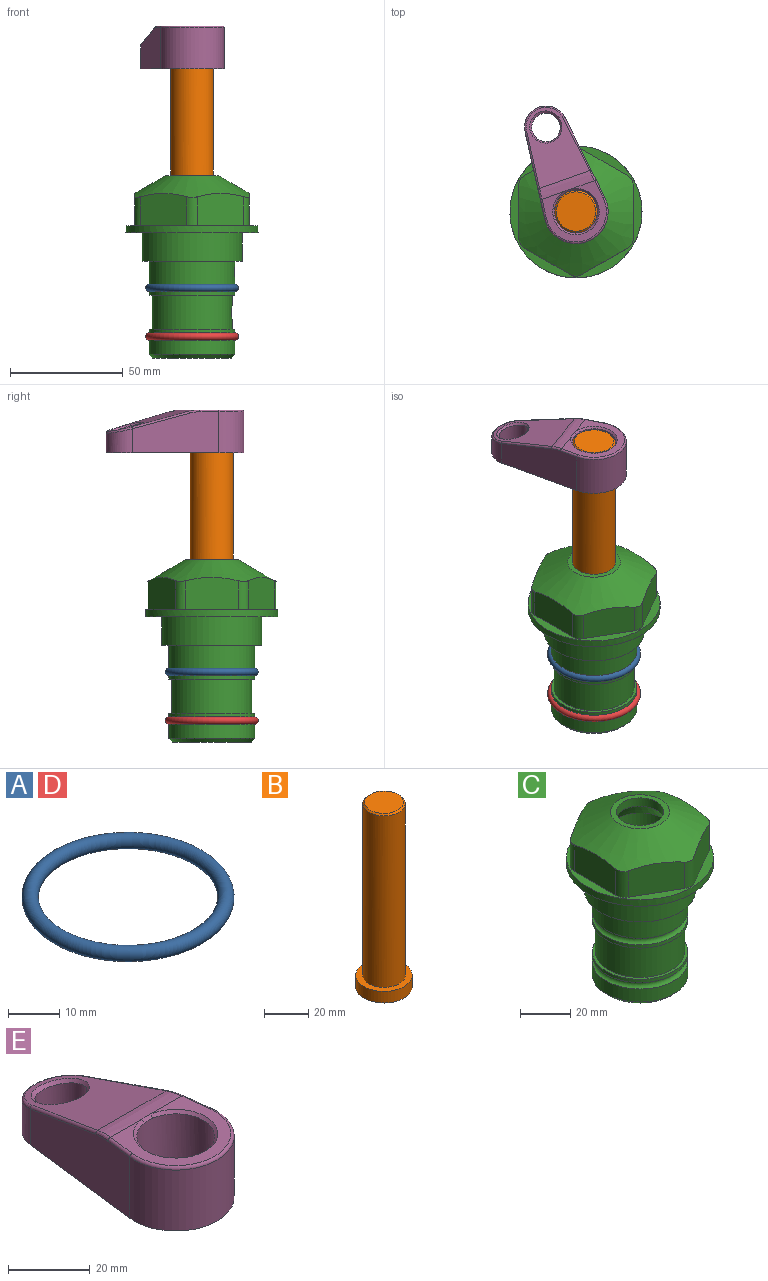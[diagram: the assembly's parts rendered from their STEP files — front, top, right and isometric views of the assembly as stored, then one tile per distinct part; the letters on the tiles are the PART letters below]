
ASSEMBLY  parts=5 mates=4
PART A: 1 faces, bbox 44.7x44.7x3.2 mm
  f0: torus R=19.05mm, axis (0,0,1), area 1193.9mm2
PART B: 6 faces, bbox 25.4x25.4x101.6 mm
  f0: plane 17.46x17.46mm, normal (0,0,1), area 239.5mm2, adj f5
  f1: plane 25.4x25.4mm, normal (0,0,-1), area 506.7mm2, adj f2
  f2: cylinder r=12.7mm len=25.4mm, axis (0,0,1), area 506.7mm2, adj f1,f3
  f3: plane 25.4x25.4mm, normal (0,0,1), area 221.7mm2, adj f2,f4
  f4: cylinder r=9.53mm len=94.46mm, axis (0,0,1), area 5653mm2, adj f3,f5
  f5: cone r=8.73mm half-angle=45deg, axis (0,0,-1), area 64.4mm2, adj f0,f4
PART C: 36 faces, bbox 58.7x58.7x81 mm
  f0: cylinder r=17.78mm len=35.56mm, axis (0,0,1), area 1670.8mm2, adj f23,f24,f31
  f1: cylinder r=19.05mm len=38.1mm, axis (0,0,1), area 1191.9mm2, adj f26,f27,f30
  f2: plane 58.66x58.66mm, normal (0,0,-1), area 1150.6mm2, adj f3,f28
  f3: cylinder r=29.33mm len=58.66mm, axis (0,0,-1), area 585.1mm2, adj f2,f4
  f4: plane 58.66x58.66mm, normal (0,0,1), area 475.9mm2, adj f3,f5,f6,f7,f8,f9,f10,f11
  f5: plane 20.32x14.34mm, normal (-0.5,0.87,0), area 324.4mm2, adj f4,f15,f16,f17
  f6: plane 20.32x14.34mm, normal (0.5,0.87,0), area 324.4mm2, adj f4,f14,f15,f17
  f7: plane 23.48x14.34mm, normal (1,0,0), area 324.4mm2, adj f4,f13,f14,f17
  f8: plane 20.32x14.34mm, normal (0.5,-0.87,0), area 324.4mm2, adj f4,f12,f13,f17
  f9: plane 20.32x14.34mm, normal (-0.5,-0.87,0), area 324.4mm2, adj f4,f11,f12,f17
  f10: plane 23.48x14.34mm, normal (-1,0,0), area 324.4mm2, adj f4,f11,f16,f17
  f11: cylinder r=5.08mm len=12.85mm, axis (0,0,-1), area 67.2mm2, adj f4,f9,f10,f17
  f12: cylinder r=5.08mm len=12.85mm, axis (0,0,-1), area 67.2mm2, adj f4,f8,f9,f17
  f13: cylinder r=5.08mm len=12.85mm, axis (0,0,-1), area 67.2mm2, adj f4,f7,f8,f17
  f14: cylinder r=5.08mm len=12.85mm, axis (0,0,-1), area 67.2mm2, adj f4,f6,f7,f17
  f15: cylinder r=5.08mm len=12.85mm, axis (0,0,-1), area 67.2mm2, adj f4,f5,f6,f17
  f16: cylinder r=5.08mm len=12.85mm, axis (0,0,-1), area 67.2mm2, adj f4,f5,f10,f17
  f17: cone r=11.73mm half-angle=60deg, axis (0,0,-1), area 2071.8mm2, adj f5,f6,f7,f8,f9,f10,f11,f12
  f18: plane 23.46x23.46mm, normal (0,0,1), area 147.4mm2, adj f17,f35
  f19: plane 34.93x34.93mm, normal (0,0,-1), area 958mm2, adj f29
  f20: cylinder r=19.05mm len=38.1mm, axis (0,0,1), area 760.1mm2, adj f21,f29
  f21: torus R=19.05mm, axis (0,0,1), area 565.3mm2, adj f20,f22
  f22: cylinder r=19.05mm len=38.1mm, axis (0,0,1), area 190mm2, adj f21,f23
  f23: plane 38.1x38.1mm, normal (0,0,1), area 146.9mm2, adj f0,f22
  f24: plane 38.1x38.1mm, normal (0,0,-1), area 146.9mm2, adj f0,f25
  f25: cylinder r=19.05mm len=38.1mm, axis (0,0,1), area 190mm2, adj f24,f26
  f26: torus R=19.05mm, axis (0,0,1), area 565.3mm2, adj f1,f25
  f27: plane 44.45x44.45mm, normal (0,0,-1), area 411.7mm2, adj f1,f28
  f28: cylinder r=22.23mm len=44.45mm, axis (0,0,1), area 1773.5mm2, adj f2,f27
  f29: cone r=19.05mm half-angle=45deg, axis (0,0,1), area 257.5mm2, adj f19,f20
  f30: cylinder r=3.17mm len=6.75mm, axis (-1,0,0), area 128mm2, adj f1,f33
  f31: cylinder r=3.17mm len=6.35mm, axis (-1,0,0), area 102.5mm2, adj f0,f33
  f32: plane 25.4x25.4mm, normal (0,0,1), area 506.7mm2, adj f33
  f33: cylinder r=12.7mm len=66.42mm, axis (0,0,-1), area 5236.2mm2, adj f30,f31,f32,f34
  f34: cone r=9.53mm half-angle=30deg, axis (0,0,-1), area 443.4mm2, adj f33,f35
  f35: cylinder r=9.53mm len=19.05mm, axis (0,0,-1), area 240.9mm2, adj f18,f34
PART D: same geometry as A
PART E: 31 faces, bbox 31.7x65.5x19.8 mm
  f0: plane 39.12x18.26mm, normal (0.99,0.12,0), area 612.2mm2, adj f1,f4,f7,f11,f13,f15
  f1: cylinder r=9.53mm len=18.91mm, axis (0,0,-1), area 296.1mm2, adj f0,f2,f7,f17
  f2: plane 39.12x18.26mm, normal (-0.99,0.12,0), area 612.2mm2, adj f1,f4,f7,f12,f14,f16
  f3: cylinder r=6.35mm len=12.7mm, axis (0,0,-1), area 362.4mm2, adj f7,f18
  f4: cylinder r=14.29mm len=28.58mm, axis (0,0,-1), area 882.2mm2, adj f0,f2,f7,f10
  f5: cylinder r=9.53mm len=19.05mm, axis (0,0,-1), area 1092.6mm2, adj f7,f19,f20
  f6: plane 26.99x23.69mm, normal (0,0,1), area 216.2mm2, adj f9,f10,f11,f12,f19
  f7: plane 63.5x28.58mm, normal (0,0,-1), area 661.8mm2, adj f0,f1,f2,f3,f4,f5,f22,f23
  f8: plane 33.52x23.6mm, normal (0,0.26,0.97), area 486mm2, adj f9,f15,f16,f17,f18
  f9: cylinder r=19.05mm len=24.72mm, axis (1,0,0), area 120.4mm2, adj f6,f8,f13,f14,f20
  f10: torus R=13.49mm, axis (0,0,1), area 59mm2, adj f4,f6,f11,f12
  f11: cylinder r=0.79mm len=8.67mm, axis (0.12,-0.99,0), area 10.8mm2, adj f0,f6,f10,f13
  f12: cylinder r=0.79mm len=8.67mm, axis (0.12,0.99,0), area 10.8mm2, adj f2,f6,f10,f14
  f13: bspline ~4.95x1.42mm, area 6.1mm2, adj f0,f9,f11,f15
  f14: bspline ~4.95x1.42mm, area 6.1mm2, adj f2,f9,f12,f16
  f15: cylinder r=0.79mm len=25.95mm, axis (0.12,-0.96,0.26), area 32.9mm2, adj f0,f8,f13,f17
  f16: cylinder r=0.79mm len=25.95mm, axis (0.12,0.96,-0.26), area 32.9mm2, adj f2,f8,f14,f17
  f17: bspline ~18.91x8.38mm, area 30mm2, adj f1,f8,f15,f16
  f18: bspline ~14.29x14.29mm, area 48.3mm2, adj f3,f8
  f19: cone r=9.53mm half-angle=45deg, axis (0,0,1), area 66.5mm2, adj f5,f6,f20
  f20: bspline ~3.22x0.96mm, area 3.5mm2, adj f5,f9,f19
  f21: plane 2.75x2.72mm, normal (0,0,-1), area 2.9mm2, adj f23,f25,f28
  f22: plane 23.05x15.88mm, normal (-0.99,-0.12,0), area 323.6mm2, adj f7,f25,f26,f27,f28,f29
  f23: plane 23.05x15.88mm, normal (0.99,-0.12,0), area 323.6mm2, adj f7,f21,f25,f27,f28,f30
  f24: cylinder r=9.53mm len=10.69mm, axis (0,0,-1), area 114.7mm2, adj f7,f27,f29,f30
  f25: cylinder r=12.7mm len=20.59mm, axis (0,0,-1), area 381.1mm2, adj f7,f21,f22,f23,f26,f28
  f26: plane 2.75x2.72mm, normal (0,0,-1), area 2.9mm2, adj f22,f25,f28
  f27: plane 19.72x18.37mm, normal (0,-0.26,-0.97), area 291.8mm2, adj f22,f23,f24,f28,f29,f30
  f28: cylinder r=15.88mm len=19.92mm, axis (1,0,0), area 54.8mm2, adj f21,f22,f23,f25,f26,f27
  f29: cylinder r=1.59mm len=11mm, axis (0,0,-1), area 34.7mm2, adj f7,f22,f24,f27
  f30: cylinder r=1.59mm len=11mm, axis (0,0,-1), area 34.7mm2, adj f7,f23,f24,f27
PLACE A at identity
PLACE B rot(axis=(0,0,1),19.6deg) t=(0,0,27.55)mm
PLACE C at identity fixed
PLACE D t=(0,0,-21.59)mm
PLACE E rot(axis=(0,0,1),19.6deg) t=(0,0,28.35)mm
MATE fastened E.f4 <-> B.f2  axis (0,0,-1) through (0,0,91.05)mm
MATE fastened C.f0 <-> D.f0  axis (0,0,1) through (0,0,-46.1)mm
MATE cylindrical C.f0 <-> B.f2  axis (0,0,1) through (0,0,-50.55)mm
MATE fastened C.f0 <-> A.f0  axis (0,0,1) through (0,0,-24.51)mm
